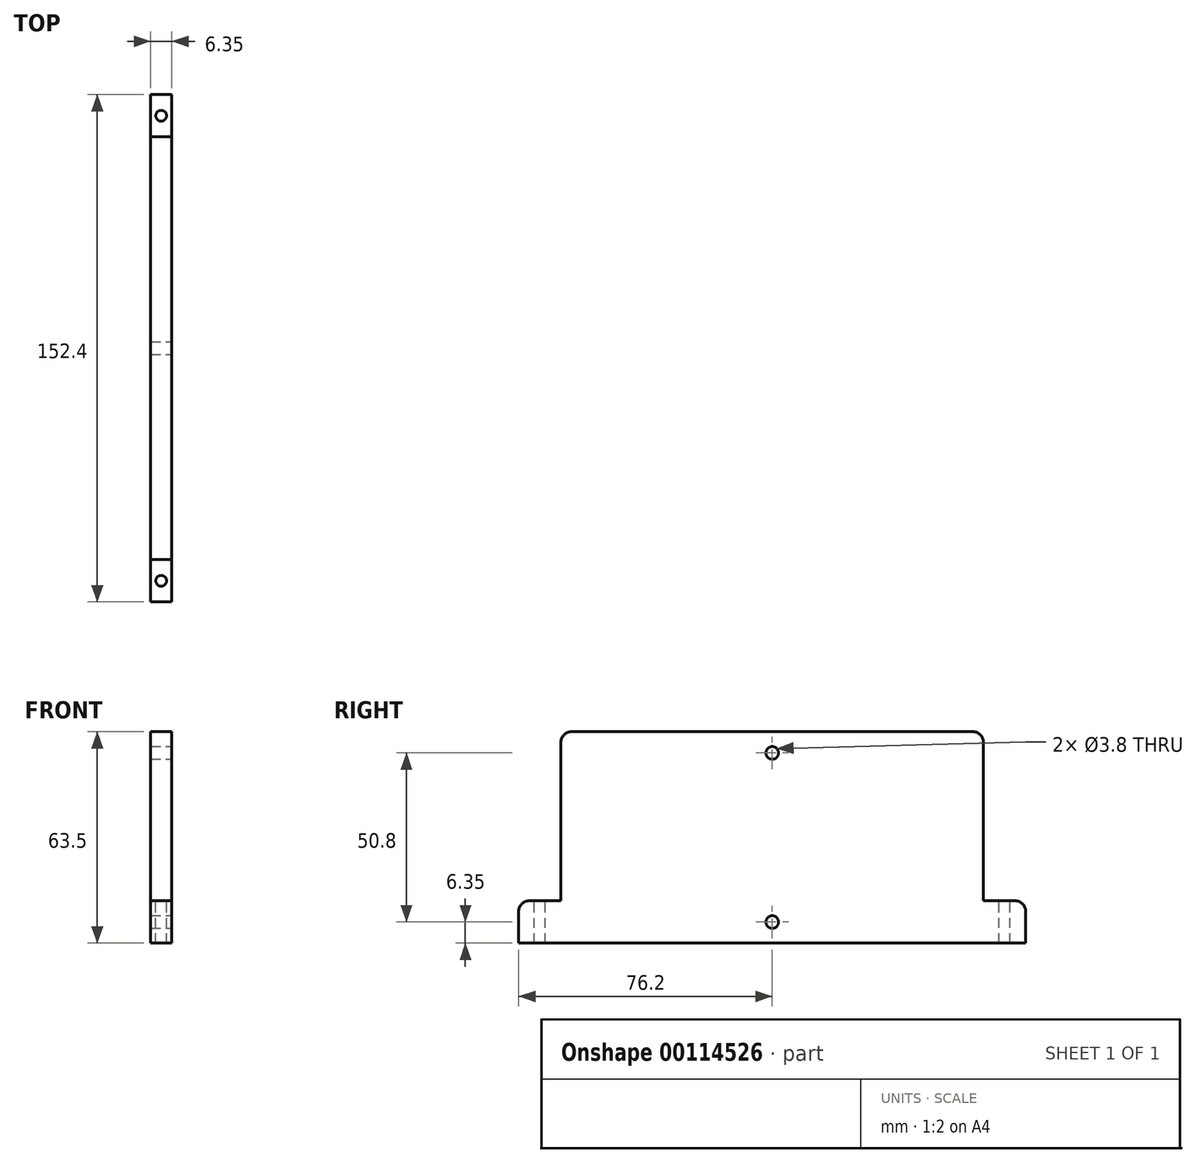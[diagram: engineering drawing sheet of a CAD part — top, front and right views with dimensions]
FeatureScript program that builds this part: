
annotation { "Feature Type Name" : "Feature", "Feature Type Description" : "" }
export const myFeature = defineFeature(function(context is Context, id is Id, definition is map)
    precondition{}
    {
        {
            var Q0;
            Q0=qCreatedBy(makeId("Right.planeOp"),FACE);
            var sketch = newSketch(context, id + "F0", { "sketchPlane" : qUnion([Q0])});
            skLineSegment(sketch, "E0.bottom", {"start": v(0, 0) * mm, "end": v(152.4, 0) * mm});
            skLineSegment(sketch, "E0.top", {"start": v(15.87, 63.5) * mm, "end": v(136.52, 63.5) * mm});
            skLineSegment(sketch, "E0.left", {"start": v(0, 0) * mm, "end": v(0, 9.52) * mm});
            skLineSegment(sketch, "E0.right", {"start": v(152.4, 0) * mm, "end": v(152.4, 9.53) * mm});
            skLineSegment(sketch, "E1", {"start": v(3.18, 12.7) * mm, "end": v(12.7, 12.7) * mm});
            skLineSegment(sketch, "E2", {"start": v(12.7, 12.7) * mm, "end": v(12.7, 60.32) * mm});
            skLineSegment(sketch, "E3", {"start": v(149.22, 12.7) * mm, "end": v(139.7, 12.7) * mm});
            skLineSegment(sketch, "E4", {"start": v(139.7, 12.7) * mm, "end": v(139.7, 60.33) * mm});
            skPoint(sketch, "E5.visualSharp", {"position": v(12.7, 63.5) * mm});
            skArc(sketch, "E5.filletArc", {"start": v(15.87, 63.5) * mm, "mid": v(13.63, 62.57) * mm, "end": v(12.7, 60.32) * mm});
            skPoint(sketch, "E6.visualSharp", {"position": v(139.7, 63.5) * mm});
            skArc(sketch, "E6.filletArc", {"start": v(139.7, 60.33) * mm, "mid": v(138.77, 62.57) * mm, "end": v(136.52, 63.5) * mm});
            skPoint(sketch, "E7.visualSharp", {"position": v(152.4, 12.7) * mm});
            skArc(sketch, "E7.filletArc", {"start": v(152.4, 9.53) * mm, "mid": v(151.47, 11.77) * mm, "end": v(149.22, 12.7) * mm});
            skPoint(sketch, "E8.visualSharp", {"position": v(0, 12.7) * mm});
            skArc(sketch, "E8.filletArc", {"start": v(3.18, 12.7) * mm, "mid": v(0.93, 11.77) * mm, "end": v(0, 9.52) * mm});
            skSolve(sketch);
        }
        {
            var Q0;
            Q0 = qSketchRegion(id + "F0", true);
            extrude(context, id + "F1", {"entities" : qUnion([Q0]), "depth" : 6.35 * mm});
        }
        {
            var Q0;
            Q0=makeQuery(id+"F1.opExtrude","CAP_FACE",FACE,{"disambiguationData":[OSD([sQuery(id+"F0.wireOp",EDGE,"E0.bottom"),sQuery(id+"F0.wireOp",EDGE,"E0.top"),sQuery(id+"F0.wireOp",EDGE,"E0.left"),sQuery(id+"F0.wireOp",EDGE,"E0.right")])],"isStart":false});
            var sketch = newSketch(context, id + "F2", { "sketchPlane" : qUnion([Q0])});
            skLineSegment(sketch, "E9", {"start": v(76.2, 63.5) * mm, "end": v(76.2, 0) * mm, "construction": true});
            skPoint(sketch, "E10", {"position": v(76.2, 57.15) * mm});
            skPoint(sketch, "E11", {"position": v(76.2, 6.35) * mm});
            skSolve(sketch);
        }
        {
            var Q0;
            Q0=sQuery(id+"F2.wireOp",VERTEX,"E10");
            var Q1;
            Q1=sQuery(id+"F2.wireOp",VERTEX,"E11");
            var Q2;
            Q2=makeQuery(id+"F1.opExtrude","SWEPT_BODY",BODY,{"disambiguationData":[OSD([sQuery(id+"F0.wireOp",EDGE,"E0.bottom"),sQuery(id+"F0.wireOp",EDGE,"E0.top"),sQuery(id+"F0.wireOp",EDGE,"E0.left"),sQuery(id+"F0.wireOp",EDGE,"E0.right")])]});
            hole(context, id + "F3", {"style" : HoleStyle.SIMPLE, "endStyle" : HoleEndStyle.THROUGH, "standardTappedOrClearance" : lookupTablePath({ "standard" : "ANSI", "fit" : "Normal (ASME)", "size" : "#6", "type" : "Clearance" }), "standardBlindInLast" : lookupTablePath({ "fit" : "Free", "standard" : "ANSI", "size" : "#6", "type" : "Clearance" }), "holeDiameter" : 3.8 * mm, "locations" : qUnion([Q0, Q1]), "scope" : qUnion([Q2]), "isTappedThrough" : true});
        }
        {
            var Q0;
            Q0=makeQuery(id+"F1.opExtrude","SWEPT_FACE",FACE,{"disambiguationData":[OSD([sQuery(id+"F0.wireOp",EDGE,"E3")])]});
            var sketch = newSketch(context, id + "F4", { "sketchPlane" : qUnion([Q0])});
            skPoint(sketch, "E12", {"position": v(3.18, 146.05) * mm});
            skPoint(sketch, "E13", {"position": v(3.18, 6.35) * mm});
            skSolve(sketch);
        }
        {
            var Q0;
            Q0=sQuery(id+"F4.wireOp",VERTEX,"E13");
            var Q1;
            Q1=sQuery(id+"F4.wireOp",VERTEX,"E12");
            var Q2;
            Q2=makeQuery(id+"F1.opExtrude","SWEPT_BODY",BODY,{"disambiguationData":[OSD([sQuery(id+"F0.wireOp",EDGE,"E0.bottom"),sQuery(id+"F0.wireOp",EDGE,"E0.top"),sQuery(id+"F0.wireOp",EDGE,"E0.left"),sQuery(id+"F0.wireOp",EDGE,"E0.right"),sQuery(id+"F0.wireOp",EDGE,"E1"),sQuery(id+"F0.wireOp",EDGE,"E2"),sQuery(id+"F0.wireOp",EDGE,"E3"),sQuery(id+"F0.wireOp",EDGE,"E4")])]});
            hole(context, id + "F5", {"style" : HoleStyle.SIMPLE, "endStyle" : HoleEndStyle.THROUGH, "standardTappedOrClearance" : lookupTablePath({ "standard" : "ANSI", "fit" : "Normal (ASME)", "size" : "#4", "type" : "Clearance" }), "standardBlindInLast" : lookupTablePath({ "fit" : "Free", "standard" : "ANSI", "size" : "#4", "type" : "Clearance" }), "holeDiameter" : 3.26 * mm, "locations" : qUnion([Q0, Q1]), "scope" : qUnion([Q2]), "isTappedThrough" : true});
        }
    });
